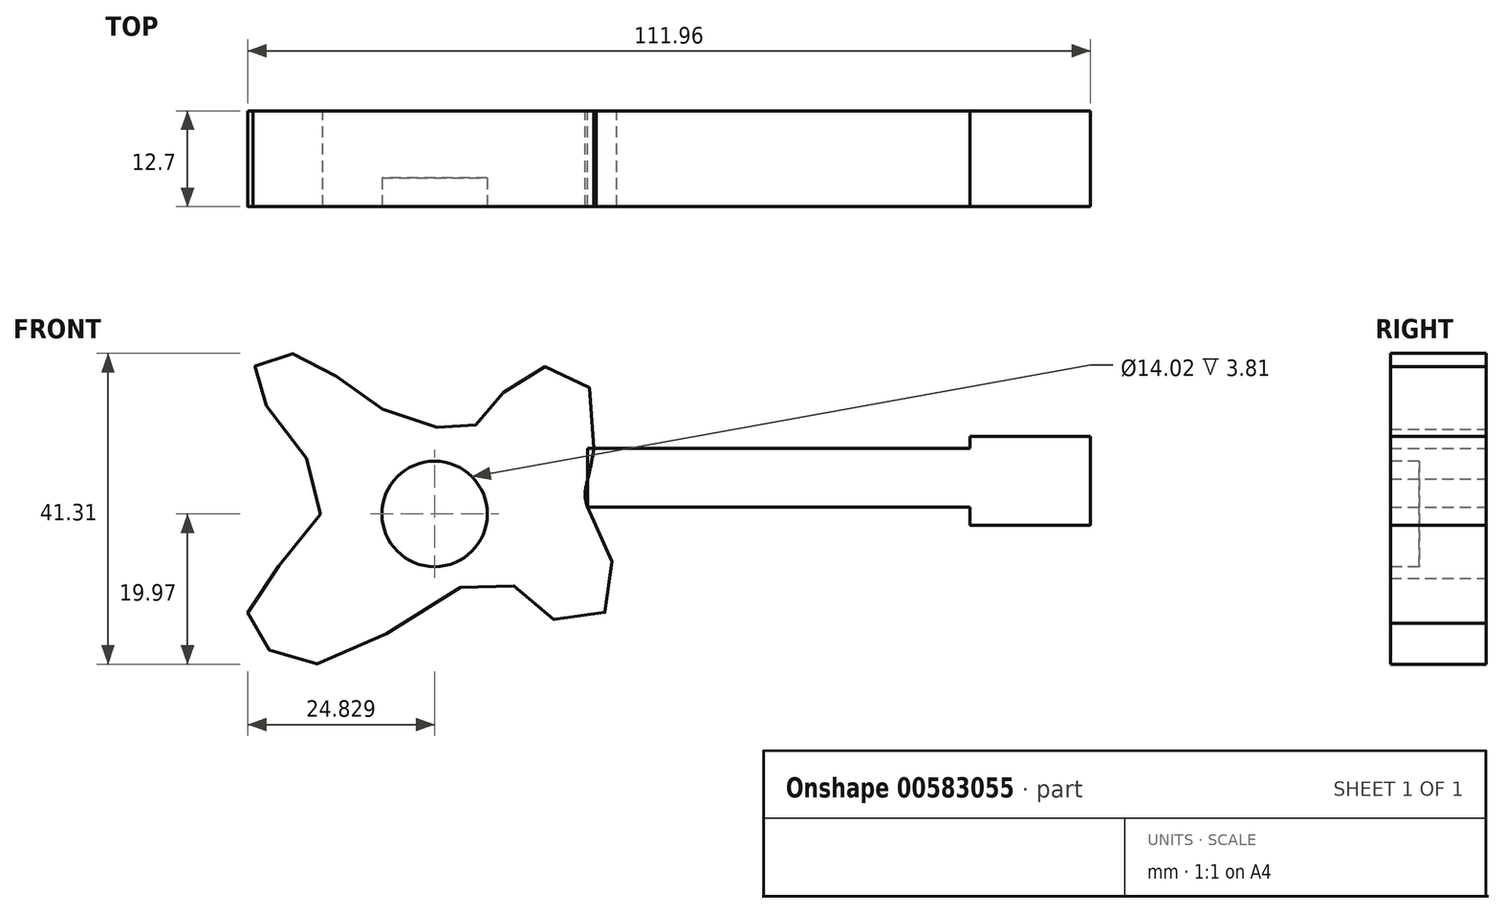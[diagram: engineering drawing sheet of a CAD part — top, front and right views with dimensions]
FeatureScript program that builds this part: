
annotation { "Feature Type Name" : "Feature", "Feature Type Description" : "" }
export const myFeature = defineFeature(function(context is Context, id is Id, definition is map)
    precondition{}
    {
        {
            var Q0;
            Q0=qCreatedBy(makeId("Front.planeOp"),FACE);
            var sketch = newSketch(context, id + "F0", { "sketchPlane" : qUnion([Q0])});
            skPoint(sketch, "E0.middle", {"position": v(0, 0) * mm});
            skFitSpline(sketch, "E1", {"points": [v(0, 0) * mm, v(0, 12.52) * mm, v(-8.37, 14.15) * mm, v(-13.9, 7.97) * mm, v(-18.45, 6.67) * mm, v(-29.5, 10.57) * mm, v(-37.96, 16.42) * mm, v(-44.14, 15.12) * mm, v(-41.86, 8.62) * mm, v(-35.36, -4.07) * mm, v(-44.79, -16.1) * mm, v(-42.83, -22.28) * mm, v(-33.08, -23.9) * mm, v(-12.27, -13.17) * mm, v(-4.47, -18.7) * mm, v(3.66, -15.77) * mm, v(0, -3.71) * mm, v(0, 0) * mm]});
            skLineSegment(sketch, "E2.bottom", {"start": v(0, -3.71) * mm, "end": v(50.8, -3.71) * mm});
            skLineSegment(sketch, "E2.top", {"start": v(0, 4.06) * mm, "end": v(50.8, 4.06) * mm});
            skLineSegment(sketch, "E2.left", {"start": v(0, -3.71) * mm, "end": v(0, 4.06) * mm});
            skLineSegment(sketch, "E2.right", {"start": v(50.8, -3.71) * mm, "end": v(50.8, 4.06) * mm});
            skLineSegment(sketch, "E3.bottom", {"start": v(50.8, -6.13) * mm, "end": v(66.78, -6.13) * mm});
            skLineSegment(sketch, "E3.top", {"start": v(50.8, 5.64) * mm, "end": v(66.78, 5.64) * mm});
            skLineSegment(sketch, "E3.left", {"start": v(50.8, -6.13) * mm, "end": v(50.8, 5.64) * mm});
            skLineSegment(sketch, "E3.right", {"start": v(66.78, -6.13) * mm, "end": v(66.78, 5.64) * mm});
            skSolve(sketch);
        }
        {
            var Q0;
            {var subQ0=sQuery(id+"F0.wireOp",EDGE,"E2.left");var subQ3=sQuery(id+"F0.wireOp",EDGE,"E2.top");var subQ6=makeQuery(id+"F0.imprint","INTERSECT",VERTEX,{"derivedFrom":[subQ3,subQ0]});Q0=makeQuery(id+"F0.imprint","IMPRINT",FACE,{"disambiguationData":[TD([[makeQuery(id+"F0.imprint","IMPRINT",EDGE,{"disambiguationData":[TD([[subQ6,-1.0]])],"derivedFrom":subQ3}),1.0]])]});}
            var Q1;
            {var subQ1=sQuery(id+"F0.wireOp",EDGE,"E2.bottom");Q1=makeQuery(id+"F0.imprint","IMPRINT",FACE,{"disambiguationData":[TD([[makeQuery(id+"F0.imprint","IMPRINT",EDGE,{"derivedFrom":subQ1}),1.0]])]});}
            var Q2;
            {var subQ3=sQuery(id+"F0.wireOp",EDGE,"E3.bottom");Q2=makeQuery(id+"F0.imprint","IMPRINT",FACE,{"disambiguationData":[TD([[makeQuery(id+"F0.imprint","IMPRINT",EDGE,{"derivedFrom":subQ3}),1.0]])]});}
            extrude(context, id + "F1", {"entities" : qUnion([Q0, Q1, Q2]), "depth" : 12.7 * mm, "offsetDistance" : 25.4 * mm});
        }
        {
            var Q0;
            Q0=makeQuery(id+"F1.opExtrude","CAP_FACE",FACE,{"disambiguationData":[OSD([sQuery(id+"F0.wireOp",EDGE,"E1"),sQuery(id+"F0.wireOp",EDGE,"E2.top"),sQuery(id+"F0.wireOp",EDGE,"E2.left")])],"isStart":false});
            var sketch = newSketch(context, id + "F2", { "sketchPlane" : qUnion([Q0])});
            skCircle(sketch, "E4", {"center": v(-20.35, -4.64) * mm, "radius": 7 * mm});
            skSolve(sketch);
        }
        {
            var Q0;
            Q0=makeQuery(id+"F2.imprint","IMPRINT",FACE,{"disambiguationData":[TD([[makeQuery(id+"F2.imprint","IMPRINT",EDGE,{"derivedFrom":sQuery(id+"F2.wireOp",EDGE,"E4")}),1.0]])]});
            extrude(context, id + "F3", {"entities" : qUnion([Q0]), "operationType" : NewBodyOperationType.REMOVE, "oppositeDirection" : true, "depth" : 3.8 * mm, "offsetDistance" : 25.4 * mm});
        }
    });
